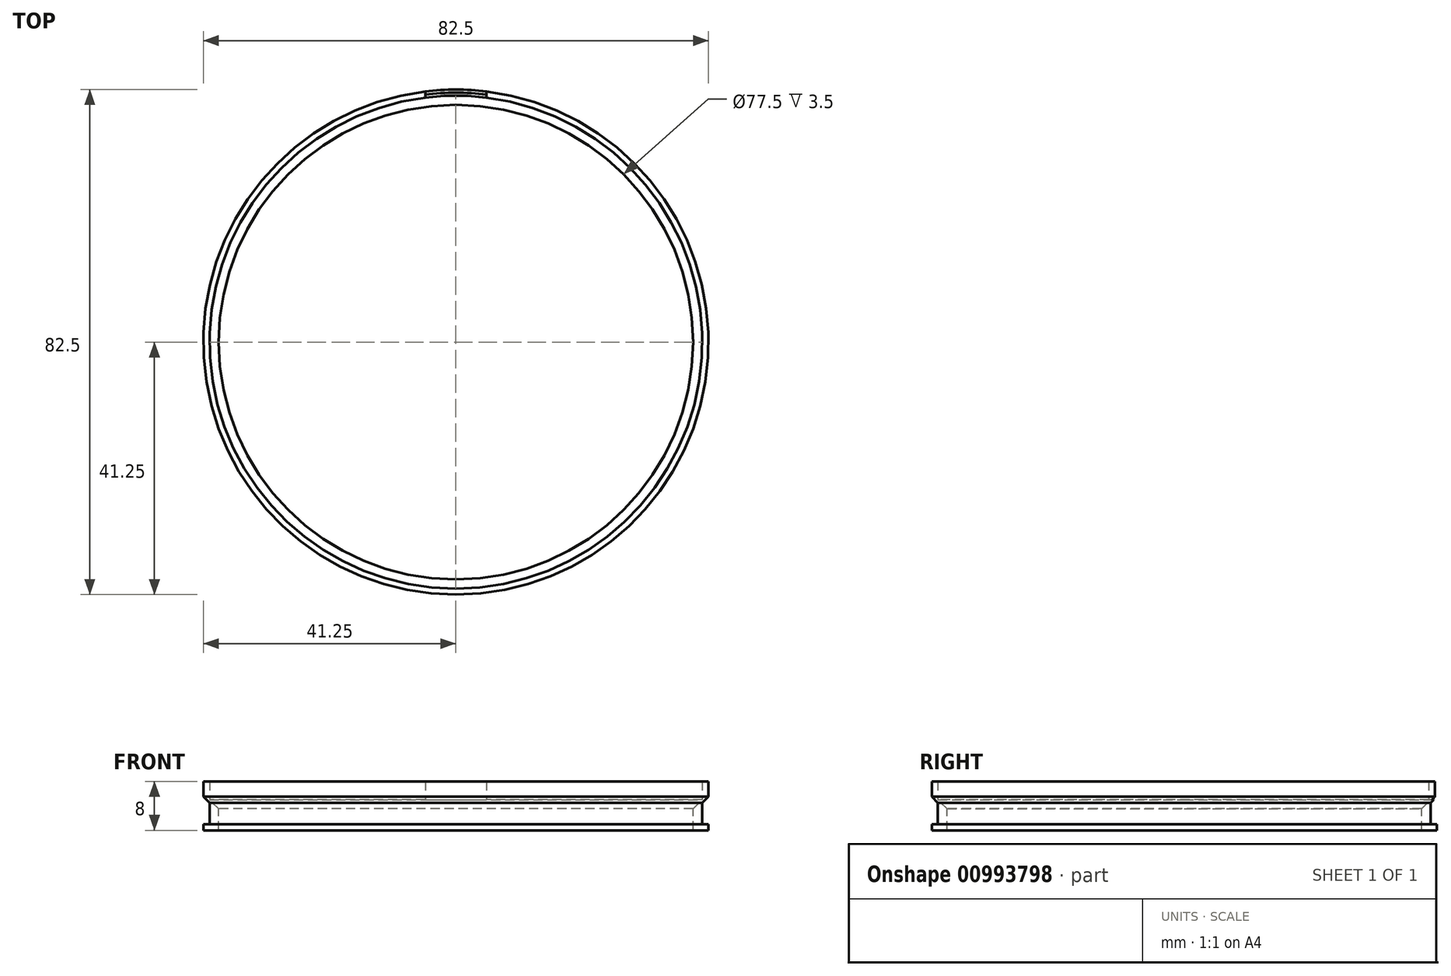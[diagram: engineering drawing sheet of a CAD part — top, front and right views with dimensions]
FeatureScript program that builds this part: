
annotation { "Feature Type Name" : "Feature", "Feature Type Description" : "" }
export const myFeature = defineFeature(function(context is Context, id is Id, definition is map)
    precondition{}
    {
        {
            var Q0;
            Q0=qCreatedBy(makeId("Top.planeOp"),FACE);
            var sketch = newSketch(context, id + "F0", { "sketchPlane" : qUnion([Q0])});
            skCircle(sketch, "E0", {"center": v(0, 0) * mm, "radius": 40.25 * mm});
            skCircle(sketch, "E1", {"center": v(0, 0) * mm, "radius": 41.25 * mm});
            skCircle(sketch, "E2", {"center": v(0, 0) * mm, "radius": 38.75 * mm});
            skSolve(sketch);
        }
        {
            var Q0;
            Q0=makeQuery(id+"F0.imprint","IMPRINT",FACE,{"disambiguationData":[TD([[makeQuery(id+"F0.imprint","IMPRINT",EDGE,{"derivedFrom":sQuery(id+"F0.wireOp",EDGE,"E0")}),-1.0]])]});
            extrude(context, id + "F1", {"entities" : qUnion([Q0]), "depth" : 3 * mm, "offsetDistance" : 25 * mm, "hasSecondDirection" : true, "secondDirectionOppositeDirection" : true, "secondDirectionDepth" : 1 * mm});
        }
        {
            var Q0;
            Q0=makeQuery(id+"F0.imprint","IMPRINT",FACE,{"disambiguationData":[TD([[makeQuery(id+"F0.imprint","IMPRINT",EDGE,{"derivedFrom":sQuery(id+"F0.wireOp",EDGE,"E0")}),1.0]])]});
            extrude(context, id + "F2", {"entities" : qUnion([Q0]), "operationType" : NewBodyOperationType.ADD, "oppositeDirection" : true, "depth" : 5 * mm, "offsetDistance" : 25 * mm});
        }
        {
            var Q0;
            Q0=makeQuery(id+"F1.opExtrude","CAP_EDGE",EDGE,{"disambiguationData":[OSD([sQuery(id+"F0.wireOp",EDGE,"E1")])],"isStart":true});
            var Q1;
            Q1=makeQuery(id+"F2.opExtrude","CAP_EDGE",EDGE,{"disambiguationData":[OSD([sQuery(id+"F0.wireOp",EDGE,"E2")])],"isStart":true});
            chamfer(context, id + "F3", {"entities" : qUnion([Q0, Q1]), "width" : 1.5 * mm, "tangentPropagation" : true});
        }
        {
            var Q0;
            Q0=makeQuery(id+"F2.opExtrude","CAP_FACE",FACE,{"disambiguationData":[OSD([sQuery(id+"F0.wireOp",EDGE,"E0"),sQuery(id+"F0.wireOp",EDGE,"E2")])],"isStart":false});
            var sketch = newSketch(context, id + "F4", { "sketchPlane" : qUnion([Q0])});
            skCircle(sketch, "E3", {"center": v(0, 0) * mm, "radius": 41.25 * mm});
            skCircle(sketch, "E4", {"center": v(0, 0) * mm, "radius": 40.25 * mm});
            skSolve(sketch);
        }
        {
            var Q0;
            Q0=makeQuery(id+"F4.imprint","IMPRINT",FACE,{"disambiguationData":[TD([[makeQuery(id+"F4.imprint","IMPRINT",EDGE,{"derivedFrom":sQuery(id+"F4.wireOp",EDGE,"E3")}),1.0]])]});
            var Q1;
            Q1=makeQuery(id+"F4.imprint","IMPRINT",FACE,{"disambiguationData":[TD([[makeQuery(id+"F4.imprint","IMPRINT",EDGE,{"derivedFrom":sQuery(id+"F4.wireOp",EDGE,"E4")}),-1.0]])]});
            extrude(context, id + "F5", {"entities" : qUnion([Q0, Q1]), "operationType" : NewBodyOperationType.ADD, "oppositeDirection" : true, "depth" : 1 * mm, "offsetDistance" : 25 * mm});
        }
        {
            var Q0;
            Q0=qCreatedBy(makeId("Front.planeOp"),FACE);
            var sketch = newSketch(context, id + "F6", { "sketchPlane" : qUnion([Q0])});
            skLineSegment(sketch, "E5.bottom", {"start": v(-5, 0) * mm, "end": v(5, 0) * mm});
            skLineSegment(sketch, "E5.top", {"start": v(-5, 3) * mm, "end": v(5, 3) * mm});
            skLineSegment(sketch, "E5.left", {"start": v(-5, 0) * mm, "end": v(-5, 3) * mm});
            skLineSegment(sketch, "E5.right", {"start": v(5, 0) * mm, "end": v(5, 3) * mm});
            skSolve(sketch);
        }
        {
            var Q0;
            Q0 = qSketchRegion(id + "F6", true);
            var Q1;
            Q1=makeQuery(id+"F1.opExtrude","SWEPT_FACE",FACE,{"disambiguationData":[OSD([sQuery(id+"F0.wireOp",EDGE,"E1")])]});
            extrude(context, id + "F7", {"entities" : qUnion([Q0]), "operationType" : NewBodyOperationType.REMOVE, "endBound" : BoundingType.UP_TO_SURFACE, "oppositeDirection" : true, "depth" : 25 * mm, "endBoundEntityFace" : qUnion([Q1]), "offsetDistance" : 25 * mm});
        }
    });
